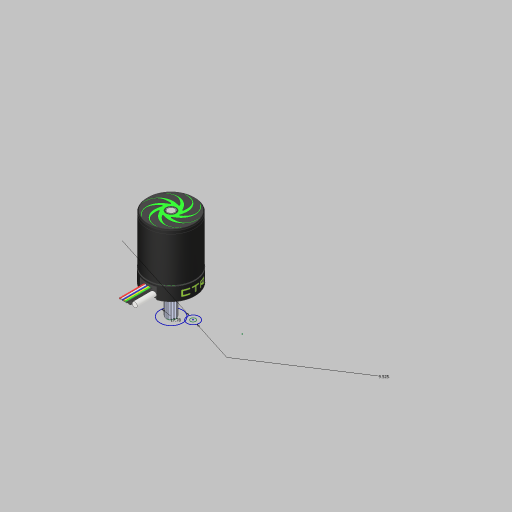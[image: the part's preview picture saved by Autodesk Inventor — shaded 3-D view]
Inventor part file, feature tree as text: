
AUTODESK INVENTOR PART (.ipt)
format: ipt  version: 2023.5 (Build 275446000, 446)  size: 2,803,200 bytes
history: native  units: in
note: dims shown in document units (in); Inventor stores cm internally (conversion verified against a paired STEP export)
features: other x33, projected_geometry x3, sketch x1
ambient origin geometry x8: Origin, YZ Plane, XZ Plane, XY Plane, X Axis, Y Axis, Z Axis, Center Point
bodies: Solid1 (feature_tree), Solid2 (feature_tree), Solid3 (feature_tree), Solid4 (feature_tree), Solid5 (feature_tree), Solid6 (feature_tree), Solid7 (feature_tree), Solid8 (feature_tree), Solid9 (feature_tree), Solid10 (feature_tree), Solid11 (feature_tree), Solid12 (feature_tree), Solid13 (feature_tree), Solid14 (feature_tree), Solid15 (feature_tree), Solid16 (feature_tree), Solid17 (feature_tree), Solid18 (feature_tree), Solid19 (feature_tree), Solid20 (feature_tree), Solid21 (feature_tree), Solid22 (feature_tree), Solid23 (feature_tree), Solid24 (feature_tree), Solid25 (feature_tree), Solid26 (feature_tree), Solid27 (feature_tree), Solid28 (feature_tree), Solid29 (feature_tree), Solid30 (feature_tree), Solid31 (feature_tree), Solid32 (feature_tree), Solid33 (feature_tree)
feature tree (37):
  sketch  "Sketch1"  dims[d0=0.375in d1=0.7in]
  other  "Faceplate-1-solid1"
  other  "Faceplate-1-solid2"
  other  "Hall effect PCB-1_Hall Effect PCB-1-solid1"
  other  "Hall effect PCB-1_SOT 23_a-1-solid1"
  other  "Hall effect PCB-1_SOT 23_a-2-solid1"
  other  "Hall effect PCB-1_SOT 23_a-3-solid1"
  other  "91595A229_Dowel Pin-1-solid1"
  other  "lamstack-1-solid1"
  other  "Magnet carrier-1-solid1"
  other  "9262K103_Oil-Resistant Buna-N O-Ring-1-solid1"
  other  "98089A247_18-8 Stainless Steel Round Shim-1-solid1"
  other  "Magnet_KJD24DIA-1-solid1"
  other  "8mm spline-1-solid1"
  other  "7804K117_Stainless Steel Ball Bearing-1-solid1"
  other  "7804K117_Stainless Steel Ball Bearing-1-solid2"
  other  "7804K117_Stainless Steel Ball Bearing-1-solid3"
  other  "7804K117_Stainless Steel Ball Bearing-1-solid4"
  other  "7804K117_Stainless Steel Ball Bearing-1-solid5"
  other  "7804K117_Stainless Steel Ball Bearing-1-solid6"
  other  "7804K117_Stainless Steel Ball Bearing-1-solid7"
  other  "7804K117_Stainless Steel Ball Bearing-1-solid8"
  other  "7804K117_Stainless Steel Ball Bearing-1-solid9"
  other  "7804K117_Stainless Steel Ball Bearing-1-solid10"
  other  "7804K117_Stainless Steel Ball Bearing-1-solid11"
  other  "7804K117_Stainless Steel Ball Bearing-1-solid12"
  other  "7804K117_Stainless Steel Ball Bearing-1-solid13"
  other  "7804K117_Stainless Steel Ball Bearing-1-solid14"
  other  "7804K117_Stainless Steel Ball Bearing-1-solid15"
  other  "7804K117_Stainless Steel Ball Bearing-1-solid16"
  other  "MR138ZZ-1-solid1"
  other  "98089A247_18-8 Stainless Steel Round Shim-2-solid1"
  other  "98541A116_External Retaining Ring-1-solid1"
  other  "rotor end cap-2-solid1"
  projected_geometry  "Project Cut Edges1"
  projected_geometry  "Project Cut Edges2"
  projected_geometry  "Project Cut Edges3"
